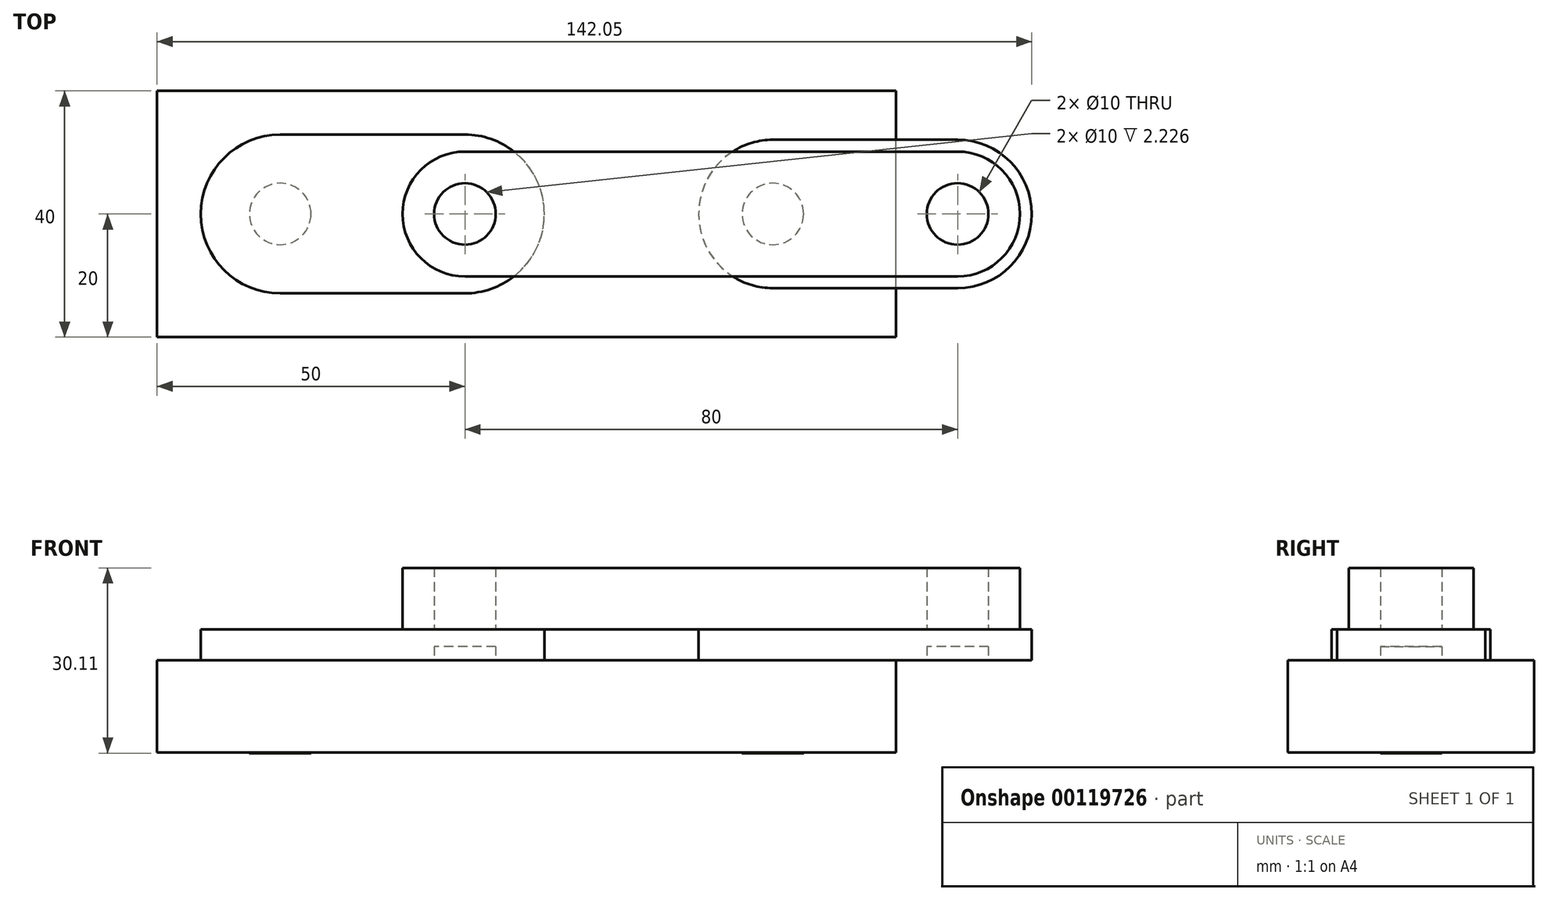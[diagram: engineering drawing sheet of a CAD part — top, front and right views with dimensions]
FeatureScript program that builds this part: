
annotation { "Feature Type Name" : "Feature", "Feature Type Description" : "" }
export const myFeature = defineFeature(function(context is Context, id is Id, definition is map)
    precondition{}
    {
        {
            var Q0;
            Q0=qCreatedBy(makeId("Front.planeOp"),FACE);
            var sketch = newSketch(context, id + "F0", { "sketchPlane" : qUnion([Q0])});
            skLineSegment(sketch, "E0.bottom", {"start": v(0, 0) * mm, "end": v(120, 0) * mm});
            skLineSegment(sketch, "E0.top", {"start": v(0, 15) * mm, "end": v(120, 15) * mm});
            skLineSegment(sketch, "E0.left", {"start": v(0, 0) * mm, "end": v(0, 15) * mm});
            skLineSegment(sketch, "E0.right", {"start": v(120, 0) * mm, "end": v(120, 15) * mm});
            skSolve(sketch);
        }
        {
            var Q0;
            Q0 = qSketchRegion(id + "F0", true);
            extrude(context, id + "F1", {"entities" : qUnion([Q0]), "endBound" : BoundingType.SYMMETRIC, "depth" : 40 * mm});
        }
        {
            var Q0;
            Q0=qCreatedBy(makeId("Top.planeOp"),FACE);
            var sketch = newSketch(context, id + "F2", { "sketchPlane" : qUnion([Q0])});
            skCircle(sketch, "E1", {"center": v(20, 0) * mm, "radius": 5 * mm});
            skCircle(sketch, "E2", {"center": v(100, 0) * mm, "radius": 5 * mm});
            skSolve(sketch);
        }
        {
            var Q0;
            Q0 = qSketchRegion(id + "F2", true);
            extrude(context, id + "F3", {"entities" : qUnion([Q0]), "operationType" : NewBodyOperationType.REMOVE, "endBound" : BoundingType.SYMMETRIC, "oppositeDirection" : true, "depth" : 100 * mm});
        }
        {
            var Q0;
            Q0=makeQuery(id+"F1.opExtrude","SWEPT_FACE",FACE,{"disambiguationData":[OSD([sQuery(id+"F0.wireOp",EDGE,"E0.top")])]});
            var sketch = newSketch(context, id + "F4", { "sketchPlane" : qUnion([Q0])});
            skCircle(sketch, "E3", {"center": v(20, 0) * mm, "radius": 5 * mm});
            skCircle(sketch, "E4", {"center": v(50, 0) * mm, "radius": 5 * mm});
            skArc(sketch, "E5", {"start": v(20, 12.9) * mm, "mid": v(7.1, 0) * mm, "end": v(20, -12.9) * mm});
            skArc(sketch, "E6", {"start": v(50, -12.9) * mm, "mid": v(62.9, 0) * mm, "end": v(50, 12.9) * mm});
            skLineSegment(sketch, "E7", {"start": v(20, 12.9) * mm, "end": v(50, 12.9) * mm});
            skLineSegment(sketch, "E8", {"start": v(20, -12.9) * mm, "end": v(50, -12.9) * mm});
            skSolve(sketch);
        }
        {
            var Q0;
            Q0 = qSketchRegion(id + "F4", true);
            extrude(context, id + "F5", {"entities" : qUnion([Q0]), "depth" : 5 * mm});
        }
        {
            var Q0;
            Q0=qCreatedBy(makeId("Top.planeOp"),FACE);
            var sketch = newSketch(context, id + "F6", { "sketchPlane" : qUnion([Q0])});
            skCircle(sketch, "E9", {"center": v(100, 0) * mm, "radius": 5 * mm});
            skCircle(sketch, "E10", {"center": v(130, 0) * mm, "radius": 5 * mm});
            skArc(sketch, "E11", {"start": v(100, 12.05) * mm, "mid": v(87.95, 0) * mm, "end": v(100, -12.05) * mm});
            skArc(sketch, "E12", {"start": v(130, -12.05) * mm, "mid": v(142.05, 0) * mm, "end": v(130, 12.05) * mm});
            skLineSegment(sketch, "E13", {"start": v(100, 12.05) * mm, "end": v(130, 12.05) * mm});
            skLineSegment(sketch, "E14", {"start": v(100, -12.05) * mm, "end": v(130, -12.05) * mm});
            skSolve(sketch);
        }
        {
            var Q0;
            Q0=makeQuery(id+"F6.imprint","IMPRINT",FACE,{"disambiguationData":[TD([[makeQuery(id+"F6.imprint","IMPRINT",EDGE,{"derivedFrom":sQuery(id+"F6.wireOp",EDGE,"E9")}),-1.0]])]});
            extrude(context, id + "F7", {"entities" : qUnion([Q0]), "depth" : 20 * mm, "hasSecondDirection" : true, "secondDirectionOppositeDirection" : false, "secondDirectionDepth" : 15 * mm});
        }
        {
            var Q0;
            Q0=qCreatedBy(makeId("Top.planeOp"),FACE);
            var sketch = newSketch(context, id + "F8", { "sketchPlane" : qUnion([Q0])});
            skCircle(sketch, "E15", {"center": v(50, 0) * mm, "radius": 5 * mm});
            skCircle(sketch, "E16", {"center": v(130, 0) * mm, "radius": 5 * mm});
            skSolve(sketch);
        }
        {
            var Q0;
            Q0 = qSketchRegion(id + "F8", true);
            extrude(context, id + "F9", {"entities" : qUnion([Q0]), "operationType" : NewBodyOperationType.ADD, "depth" : 30 * mm, "hasSecondDirection" : true, "secondDirectionOppositeDirection" : false, "secondDirectionDepth" : 17.23 * mm});
        }
        {
            var Q0;
            Q0=qCreatedBy(makeId("Top.planeOp"),FACE);
            var sketch = newSketch(context, id + "F10", { "sketchPlane" : qUnion([Q0])});
            skCircle(sketch, "E17", {"center": v(20, 0) * mm, "radius": 5 * mm});
            skCircle(sketch, "E18", {"center": v(100, 0) * mm, "radius": 5 * mm});
            skSolve(sketch);
        }
        {
            var Q0;
            Q0 = qSketchRegion(id + "F10", true);
            extrude(context, id + "F11", {"entities" : qUnion([Q0]), "operationType" : NewBodyOperationType.ADD, "depth" : 20 * mm, "hasSecondDirection" : true, "secondDirectionOppositeDirection" : true, "secondDirectionDepth" : 0.1 * mm});
        }
        {
            var Q0;
            Q0=qCreatedBy(makeId("Top.planeOp"),FACE);
            var sketch = newSketch(context, id + "F12", { "sketchPlane" : qUnion([Q0])});
            skCircle(sketch, "E19", {"center": v(50, 0) * mm, "radius": 5 * mm});
            skCircle(sketch, "E20", {"center": v(130, 0) * mm, "radius": 5 * mm});
            skArc(sketch, "E21", {"start": v(50, 10.14) * mm, "mid": v(39.86, 0) * mm, "end": v(50, -10.14) * mm});
            skArc(sketch, "E22", {"start": v(130, -10.14) * mm, "mid": v(140.14, 0) * mm, "end": v(130, 10.14) * mm});
            skLineSegment(sketch, "E23", {"start": v(50, 10.14) * mm, "end": v(130, 10.14) * mm});
            skLineSegment(sketch, "E24", {"start": v(130, -10.14) * mm, "end": v(50, -10.14) * mm});
            skSolve(sketch);
        }
        {
            var Q0;
            Q0 = qSketchRegion(id + "F12", true);
            extrude(context, id + "F13", {"entities" : qUnion([Q0]), "depth" : 30 * mm, "hasSecondDirection" : true, "secondDirectionOppositeDirection" : false, "secondDirectionDepth" : 20 * mm});
        }
    });
